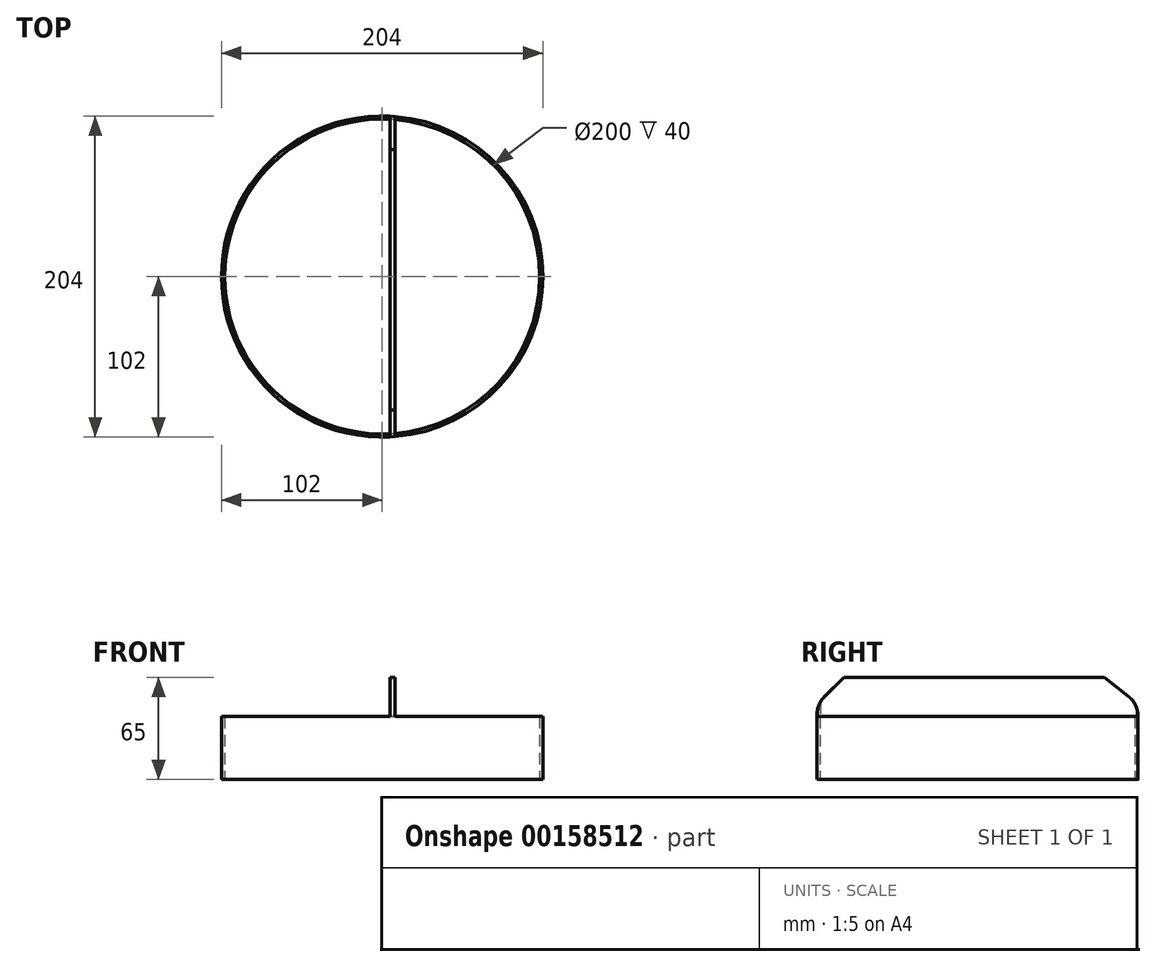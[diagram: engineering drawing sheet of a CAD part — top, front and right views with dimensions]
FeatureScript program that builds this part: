
annotation { "Feature Type Name" : "Feature", "Feature Type Description" : "" }
export const myFeature = defineFeature(function(context is Context, id is Id, definition is map)
    precondition{}
    {
        {
            var Q0;
            Q0=qCreatedBy(makeId("Top.planeOp"),FACE);
            var sketch = newSketch(context, id + "F0", { "sketchPlane" : qUnion([Q0])});
            skCircle(sketch, "E0", {"center": v(0, 0) * mm, "radius": 100 * mm});
            skCircle(sketch, "E1.0", {"center": v(0, 0) * mm, "radius": 102 * mm});
            skLineSegment(sketch, "E2", {"start": v(0, 0) * mm, "end": v(0, -102) * mm, "construction": true});
            skLineSegment(sketch, "E3", {"start": v(0, -102) * mm, "end": v(0, 102) * mm, "construction": true});
            skSolve(sketch);
        }
        {
            var Q0;
            Q0=makeQuery(id+"F0.imprint","IMPRINT",FACE,{"disambiguationData":[TD([[makeQuery(id+"F0.imprint","IMPRINT",EDGE,{"derivedFrom":sQuery(id+"F0.wireOp",EDGE,"E0")}),-1.0]])]});
            extrude(context, id + "F1", {"entities" : qUnion([Q0]), "depth" : 25 * mm, "offsetDistance" : 25 * mm});
        }
        {
            var Q0;
            Q0=makeQuery(id+"F1.opExtrude","CAP_FACE",FACE,{"disambiguationData":[OSD([sQuery(id+"F0.wireOp",EDGE,"E0"),sQuery(id+"F0.wireOp",EDGE,"E1.0")])],"isStart":false});
            var sketch = newSketch(context, id + "F2", { "sketchPlane" : qUnion([Q0])});
            skLineSegment(sketch, "E4.0", {"start": v(0, -102) * mm, "end": v(0, 102) * mm, "construction": true});
            skLineSegment(sketch, "E5", {"start": v(0, -100) * mm, "end": v(5, -99.88) * mm});
            skLineSegment(sketch, "E6", {"start": v(5, -99.87) * mm, "end": v(5.05, -101.87) * mm});
            skLineSegment(sketch, "E7", {"start": v(5.05, -101.87) * mm, "end": v(8.04, -101.68) * mm});
            skLineSegment(sketch, "E8", {"start": v(8.04, -101.68) * mm, "end": v(8.04, 101.68) * mm});
            skLineSegment(sketch, "E9", {"start": v(8.04, 101.68) * mm, "end": v(5.05, 101.87) * mm});
            skLineSegment(sketch, "E10", {"start": v(5.05, 101.87) * mm, "end": v(5, -99.87) * mm});
            skSolve(sketch);
        }
        {
            var Q0;
            {var subQ0=sQuery(id+"F2.wireOp",EDGE,"E8");var subQ1=makeQuery(id+"F1.opExtrude","CAP_EDGE",EDGE,{"disambiguationData":[OSD([sQuery(id+"F0.wireOp",EDGE,"E0")])],"isStart":false});var subQ2=makeQuery(id+"F2.imprint","INTERSECT",VERTEX,{"disambiguationData":[OD(0.0)],"derivedFrom":[subQ1,subQ0]});Q0=makeQuery(id+"F2.imprint","IMPRINT",FACE,{"disambiguationData":[TD([[makeQuery(id+"F2.imprint","IMPRINT",EDGE,{"disambiguationData":[TD([[subQ2,-1.0]])],"derivedFrom":subQ0}),1.0]])]});}
            var Q1;
            {var subQ0=sQuery(id+"F2.wireOp",EDGE,"E6");Q1=makeQuery(id+"F2.imprint","IMPRINT",FACE,{"disambiguationData":[TD([[makeQuery(id+"F2.imprint","IMPRINT",EDGE,{"derivedFrom":subQ0}),1.0]])]});}
            var Q2;
            {var subQ0=sQuery(id+"F2.wireOp",EDGE,"E9");Q2=makeQuery(id+"F2.imprint","IMPRINT",FACE,{"disambiguationData":[TD([[makeQuery(id+"F2.imprint","IMPRINT",EDGE,{"derivedFrom":subQ0}),1.0]])]});}
            extrude(context, id + "F3", {"entities" : qUnion([Q0, Q1, Q2]), "operationType" : NewBodyOperationType.ADD, "depth" : 25 * mm, "offsetDistance" : 25 * mm});
        }
        {
            var Q0;
            Q0=makeQuery(id+"F3.opExtrude","SWEPT_FACE",FACE,{"disambiguationData":[OSD([sQuery(id+"F2.wireOp",EDGE,"E6")])]});
            var sketch = newSketch(context, id + "F4", { "sketchPlane" : qUnion([Q0])});
            skLineSegment(sketch, "E11", {"start": v(101.97, 25) * mm, "end": v(101.97, 33) * mm});
            skLineSegment(sketch, "E12", {"start": v(101.97, 33) * mm, "end": v(84.97, 50) * mm});
            skLineSegment(sketch, "E13", {"start": v(99.97, 35) * mm, "end": v(99.97, 50) * mm});
            skLineSegment(sketch, "E14", {"start": v(99.97, 50) * mm, "end": v(84.97, 50) * mm});
            skLineSegment(sketch, "E15.0", {"start": v(-101.72, 50) * mm, "end": v(-101.72, 25) * mm});
            skLineSegment(sketch, "E16", {"start": v(-101.72, 25) * mm, "end": v(-101.72, 33) * mm});
            skLineSegment(sketch, "E17", {"start": v(-101.72, 33) * mm, "end": v(-80.38, 50) * mm});
            skLineSegment(sketch, "E18", {"start": v(-80.38, 50) * mm, "end": v(-80.38, 25) * mm});
            skLineSegment(sketch, "E19", {"start": v(-80.38, 25) * mm, "end": v(-101.72, 25) * mm});
            skLineSegment(sketch, "E20", {"start": v(-101.72, 50) * mm, "end": v(-80.38, 50) * mm});
            skSolve(sketch);
        }
        {
            var Q0;
            {var subQ2=sQuery(id+"F4.wireOp",EDGE,"E13");Q0=makeQuery(id+"F4.imprint","IMPRINT",FACE,{"disambiguationData":[TD([[makeQuery(id+"F4.imprint","IMPRINT",EDGE,{"derivedFrom":subQ2}),-1.0]])]});}
            var Q1;
            {var subQ4=sQuery(id+"F4.wireOp",EDGE,"E13");Q1=makeQuery(id+"F4.imprint","IMPRINT",FACE,{"disambiguationData":[TD([[makeQuery(id+"F4.imprint","IMPRINT",EDGE,{"derivedFrom":subQ4}),1.0]])]});}
            extrude(context, id + "F5", {"entities" : qUnion([Q0, Q1]), "operationType" : NewBodyOperationType.REMOVE, "oppositeDirection" : true, "depth" : 25 * mm, "offsetDistance" : 25 * mm});
        }
        {
            var Q0;
            Q0=makeQuery(id+"F4.imprint","IMPRINT",FACE,{"disambiguationData":[TD([[makeQuery(id+"F4.imprint","IMPRINT",EDGE,{"derivedFrom":sQuery(id+"F4.wireOp",EDGE,"E15.0")}),1.0]])]});
            extrude(context, id + "F6", {"entities" : qUnion([Q0]), "operationType" : NewBodyOperationType.REMOVE, "oppositeDirection" : true, "depth" : 25 * mm, "offsetDistance" : 25 * mm});
        }
        {
            var Q0;
            Q0=makeQuery(id+"F6.boolean.opBoolean","COPY",EDGE,{"derivedFrom":makeQuery(id+"F6.opExtrude","SWEPT_EDGE",EDGE,{"disambiguationData":[OSD([sQuery(id+"F4.wireOp",EDGE,"E17"),sQuery(id+"F4.wireOp",EDGE,"E18"),sQuery(id+"F4.wireOp",EDGE,"E20")])]})});
            var Q1;
            Q1=makeQuery(id+"F6.boolean.opBoolean","INTERSECT",EDGE,{"derivedFrom":[makeQuery(id+"F3.opExtrude","SWEPT_FACE",FACE,{"disambiguationData":[OSD([sQuery(id+"F2.wireOp",EDGE,"E9")])]}),makeQuery(id+"F6.opExtrude","SWEPT_FACE",FACE,{"disambiguationData":[OSD([sQuery(id+"F4.wireOp",EDGE,"E17")])]})]});
            var Q2;
            Q2=makeQuery(id+"F5.boolean.opBoolean","COPY",EDGE,{"derivedFrom":makeQuery(id+"F5.opExtrude","SWEPT_EDGE",EDGE,{"disambiguationData":[OSD([sQuery(id+"F4.wireOp",EDGE,"E12"),sQuery(id+"F4.wireOp",EDGE,"E14")])]})});
            var Q3;
            Q3=makeQuery(id+"F5.boolean.opBoolean","INTERSECT",EDGE,{"derivedFrom":[makeQuery(id+"F3.opExtrude","SWEPT_FACE",FACE,{"disambiguationData":[OSD([sQuery(id+"F2.wireOp",EDGE,"E7")])]}),makeQuery(id+"F5.opExtrude","SWEPT_FACE",FACE,{"disambiguationData":[OSD([sQuery(id+"F4.wireOp",EDGE,"E12")])]})]});
            fillet(context, id + "F7", {"entities" : qUnion([Q0, Q1, Q2, Q3]), "radius" : 15 * mm, "tangentPropagation" : true, "allowEdgeOverflow" : false});
        }
        {
            var Q0;
            Q0=makeQuery(id+"F0.imprint","IMPRINT",FACE,{"disambiguationData":[TD([[makeQuery(id+"F0.imprint","IMPRINT",EDGE,{"derivedFrom":sQuery(id+"F0.wireOp",EDGE,"E0")}),-1.0]])]});
            extrude(context, id + "F8", {"entities" : qUnion([Q0]), "operationType" : NewBodyOperationType.ADD, "oppositeDirection" : true, "depth" : 15 * mm, "offsetDistance" : 25 * mm});
        }
    });
